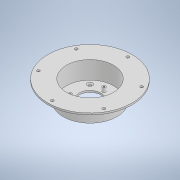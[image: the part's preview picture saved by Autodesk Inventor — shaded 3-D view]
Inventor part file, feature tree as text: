
AUTODESK INVENTOR PART (.ipt)
format: ipt  version: 2021 (Build 250183000, 183)  size: 204,800 bytes
history: native  units: in
note: dims shown in document units (in); Inventor stores cm internally (conversion verified against a paired STEP export)
features: sketch x5, hole x3, projected_geometry x3, revolve x1, fillet x1, extrude x1
ambient origin geometry x8: Origin, YZ Plane, XZ Plane, XY Plane, X Axis, Y Axis, Z Axis, Center Point
bodies: Solid1 (feature_tree)
feature tree (14):
  revolve  "Revolution1"  [1 undecoded]
  hole  "Hole1"  [1 undecoded]
  hole  "Hole2"  [1 undecoded]
  fillet  "Fillet1"  Radius=1.2205in
  extrude  "Extrusion1"  Depth=0.0787in
  hole  "Hole3"  [1 undecoded]
  sketch  "Sketch1"  dims[d0=0.0787in d1=0.0787in]
  sketch  "Sketch2"  dims[d4=1.9685in d7=0.5118in]
  sketch  "Sketch3"  dims[d10=90.0deg d11=0.7559in d14=1.2205in]
  sketch  "Sketch4"  dims[d15=1.2205in]
  sketch  "Sketch5"  dims[d16=0.1339in d17=0.1969in d18=0.248in d19=0.0787in d20=90.0deg d21=0.2559in d22=0.8108in d23=3.5433in d24=2.3622in d26=360.0deg d28=0.1339in d29=0.1969in d30=0.248in d31=0.0787in d32=90.0deg d33=0.2559in d34=0.8108in d35=1.2598in d36=0.1575in d37=0.8346in d38=0.1969in d39=0.1575in d45=0.187in d46=0.0in d47=0.0617in d48=0.1575in d49=0.248in d50=0.0787in d51=90.0deg d52=0.248in d53=0.8108in d54=0.6535in d55=0.1575in d56=0.9843in d57=0.4331in]
  projected_geometry  "Projected Loop1"
  projected_geometry  "Projected Loop4"
  projected_geometry  "Projected Loop5"
note: 4 required parameter values undecoded (feature->parameter linkage not recoverable at this tier; creation-order binding heuristic only, values carry confidence <= 0.55)